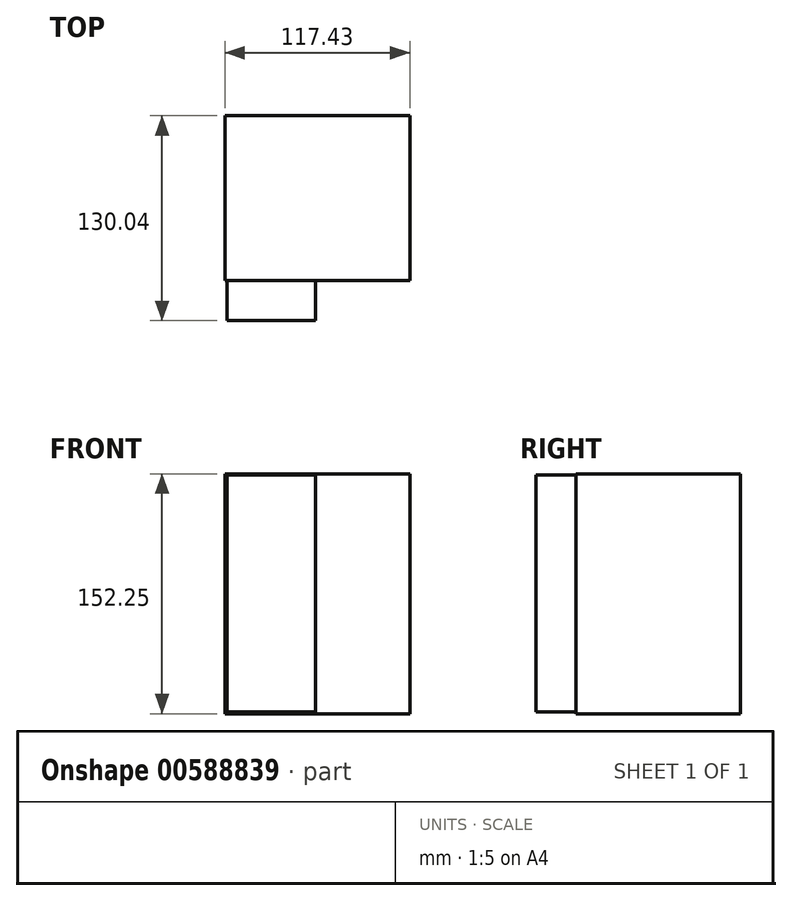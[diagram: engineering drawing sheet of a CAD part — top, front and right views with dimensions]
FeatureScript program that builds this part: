
annotation { "Feature Type Name" : "Feature", "Feature Type Description" : "" }
export const myFeature = defineFeature(function(context is Context, id is Id, definition is map)
    precondition{}
    {
        {
            var Q0;
            Q0=qCreatedBy(makeId("Front.planeOp"),FACE);
            var sketch = newSketch(context, id + "F0", { "sketchPlane" : qUnion([Q0])});
            skLineSegment(sketch, "E0.bottom", {"start": v(-61.45, 76.7) * mm, "end": v(55.98, 76.7) * mm});
            skLineSegment(sketch, "E0.top", {"start": v(-61.45, -75.55) * mm, "end": v(55.98, -75.55) * mm});
            skLineSegment(sketch, "E0.left", {"start": v(-61.45, 76.7) * mm, "end": v(-61.45, -75.55) * mm});
            skLineSegment(sketch, "E0.right", {"start": v(55.98, 76.7) * mm, "end": v(55.98, -75.55) * mm});
            skSolve(sketch);
        }
        {
            var Q0;
            Q0=makeQuery(id+"F0.imprint","IMPRINT",FACE,{"disambiguationData":[TD([[makeQuery(id+"F0.imprint","IMPRINT",EDGE,{"derivedFrom":sQuery(id+"F0.wireOp",EDGE,"E0.bottom")}),-1.0]])]});
            extrude(context, id + "F1", {"entities" : qUnion([Q0]), "endBound" : BoundingType.SYMMETRIC, "depth" : 104.65 * mm, "offsetDistance" : 25.4 * mm});
        }
        {
            var Q0;
            Q0=makeQuery(id+"F1.opExtrude","CAP_FACE",FACE,{"disambiguationData":[OSD([sQuery(id+"F0.wireOp",EDGE,"E0.bottom"),sQuery(id+"F0.wireOp",EDGE,"E0.top"),sQuery(id+"F0.wireOp",EDGE,"E0.left"),sQuery(id+"F0.wireOp",EDGE,"E0.right")])],"isStart":false});
            var sketch = newSketch(context, id + "F2", { "sketchPlane" : qUnion([Q0])});
            skSolve(sketch);
        }
        {
            var Q0;
            Q0=makeQuery(id+"F2.imprint","IMPRINT",FACE,{"disambiguationData":[TD([[makeQuery(id+"F2.imprint","IMPRINT",EDGE,{"derivedFrom":makeQuery(id+"F1.opExtrude","CAP_EDGE",EDGE,{"disambiguationData":[OSD([sQuery(id+"F0.wireOp",EDGE,"E0.bottom")])],"isStart":false})}),-1.0]])]});
            var sketch = newSketch(context, id + "F3", { "sketchPlane" : qUnion([Q0])});
            skLineSegment(sketch, "E1.bottom", {"start": v(-60.2, 76.05) * mm, "end": v(-3.9, 76.05) * mm});
            skLineSegment(sketch, "E1.top", {"start": v(-60.2, -74.4) * mm, "end": v(-3.9, -74.4) * mm});
            skLineSegment(sketch, "E1.left", {"start": v(-60.2, 76.05) * mm, "end": v(-60.2, -74.4) * mm});
            skLineSegment(sketch, "E1.right", {"start": v(-3.9, 76.05) * mm, "end": v(-3.9, -74.4) * mm});
            skSolve(sketch);
        }
        {
            var Q0;
            Q0 = qSketchRegion(id + "F3", true);
            extrude(context, id + "F4", {"entities" : qUnion([Q0]), "operationType" : NewBodyOperationType.ADD, "depth" : 25.4 * mm, "offsetDistance" : 25.4 * mm});
        }
    });
